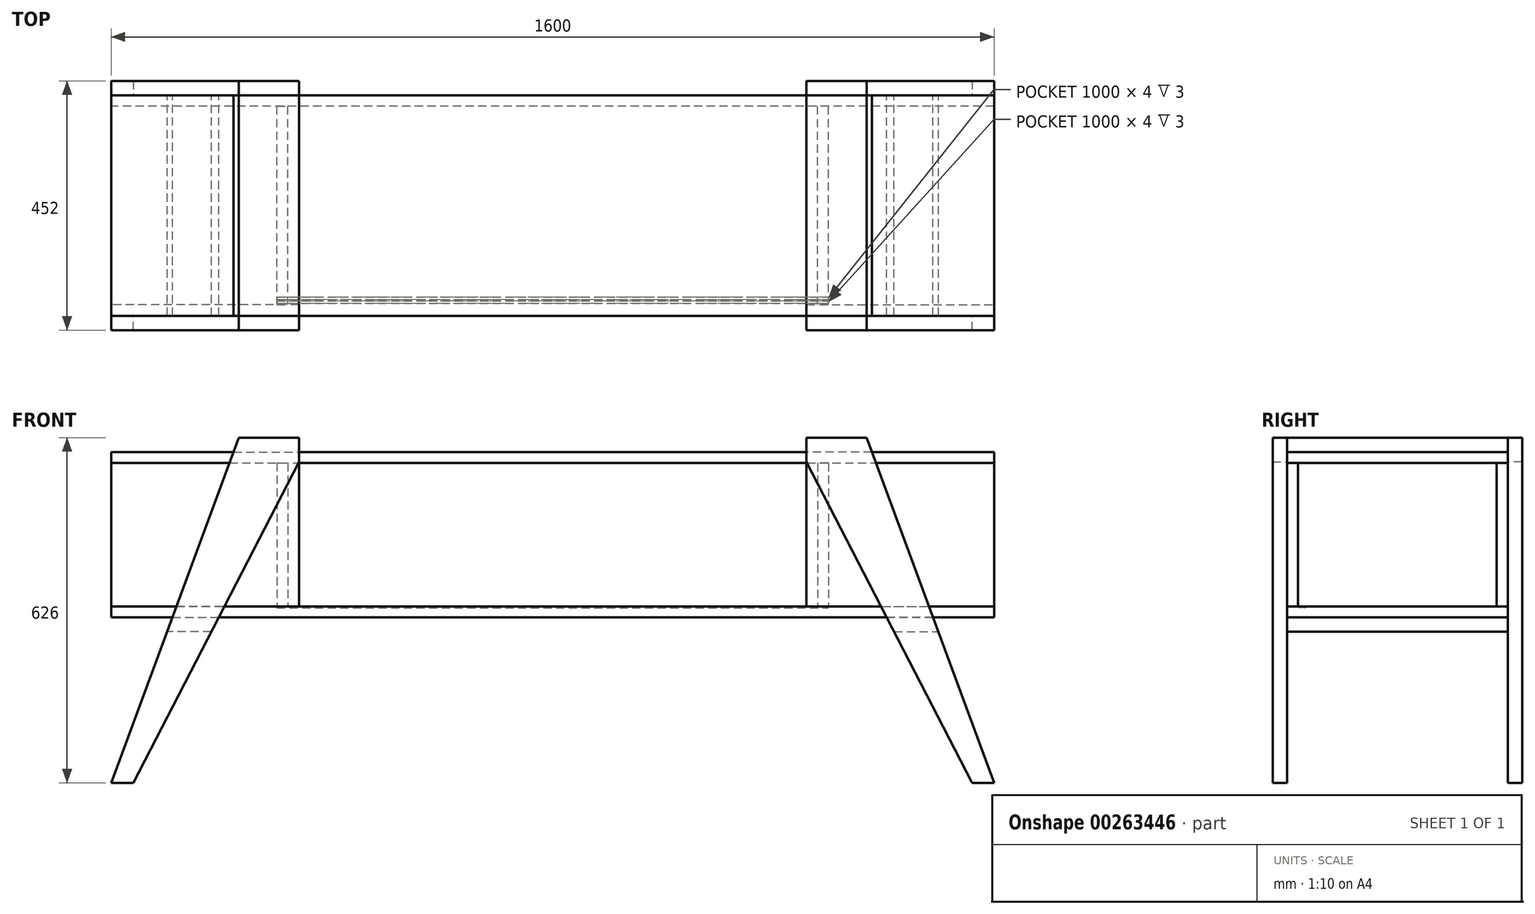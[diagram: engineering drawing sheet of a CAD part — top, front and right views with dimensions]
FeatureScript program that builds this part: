
annotation { "Feature Type Name" : "Feature", "Feature Type Description" : "" }
export const myFeature = defineFeature(function(context is Context, id is Id, definition is map)
    precondition{}
    {
        {
            assignVariable(context, id + "F0", {"name" : "Long", "anyValue" : 1600});
        }
        {
            assignVariable(context, id + "F1", {"name" : "Prof", "anyValue" : 400});
        }
        {
            assignVariable(context, id + "F2", {"name" : "EpP", "anyValue" : 20});
        }
        {
            assignVariable(context, id + "F3", {"name" : "EpFoot", "anyValue" : 26});
        }
        {
            assignVariable(context, id + "F4", {"name" : "EpPortes", "anyValue" : 3});
        }
        {
            var Q0;
            Q0=qCreatedBy(makeId("Front.planeOp"),FACE);
            var sketch = newSketch(context, id + "F5", { "sketchPlane" : qUnion([Q0])});
            skLineSegment(sketch, "E0.bottom", {"start": v(-800, 580) * mm, "end": v(800, 580) * mm});
            skLineSegment(sketch, "E0.top", {"start": v(-800, 600) * mm, "end": v(800, 600) * mm});
            skLineSegment(sketch, "E0.left", {"start": v(-800, 580) * mm, "end": v(-800, 600) * mm});
            skLineSegment(sketch, "E0.right", {"start": v(800, 580) * mm, "end": v(800, 600) * mm});
            skLineSegment(sketch, "E1", {"start": v(-1523.7, 450) * mm, "end": v(1632.53, 450) * mm, "construction": true});
            skLineSegment(sketch, "E2.MirrorCS", {"start": v(-800, 320) * mm, "end": v(-800, 300) * mm});
            skLineSegment(sketch, "E3.MirrorCS", {"start": v(800, 320) * mm, "end": v(800, 300) * mm});
            skLineSegment(sketch, "E4.MirrorCS", {"start": v(-800, 300) * mm, "end": v(800, 300) * mm});
            skLineSegment(sketch, "E5.MirrorCS", {"start": v(-800, 320) * mm, "end": v(800, 320) * mm});
            skSolve(sketch);
        }
        {
            var Q0;
            Q0=qSketchRegion(id+"F5",true);
            extrude(context, id + "F6", {"entities" : qUnion([Q0]), "endBound" : BoundingType.SYMMETRIC, "depth" : (getVariable(context, 'Prof')) * mm});
        }
        {
            var Q0;
            Q0=qCreatedBy(makeId("Right.planeOp"),FACE);
            var sketch = newSketch(context, id + "F7", { "sketchPlane" : qUnion([Q0])});
            skLineSegment(sketch, "E6.bottom", {"start": v(200, 580) * mm, "end": v(180, 580) * mm});
            skLineSegment(sketch, "E6.top", {"start": v(200, 320) * mm, "end": v(180, 320) * mm});
            skLineSegment(sketch, "E6.left", {"start": v(200, 580) * mm, "end": v(200, 320) * mm});
            skLineSegment(sketch, "E6.right", {"start": v(180, 580) * mm, "end": v(180, 320) * mm});
            skSolve(sketch);
        }
        {
            var Q0;
            Q0=qSketchRegion(id+"F7",true);
            extrude(context, id + "F8", {"entities" : qUnion([Q0]), "endBound" : BoundingType.SYMMETRIC, "depth" : getVariable(context, 'Long') * mm});
        }
        {
            var Q0;
            Q0=qCreatedBy(makeId("Front.planeOp"),FACE);
            var sketch = newSketch(context, id + "F9", { "sketchPlane" : qUnion([Q0])});
            skLineSegment(sketch, "E7.bottom", {"start": v(-500, 580) * mm, "end": v(-480, 580) * mm});
            skLineSegment(sketch, "E7.top", {"start": v(-500, 320) * mm, "end": v(-480, 320) * mm});
            skLineSegment(sketch, "E7.left", {"start": v(-500, 580) * mm, "end": v(-500, 320) * mm});
            skLineSegment(sketch, "E7.right", {"start": v(-480, 580) * mm, "end": v(-480, 320) * mm});
            skSolve(sketch);
        }
        {
            var Q0;
            Q0=qSketchRegion(id+"F9",true);
            extrude(context, id + "F10", {"entities" : qUnion([Q0]), "endBound" : BoundingType.SYMMETRIC, "depth" : (getVariable(context, 'Prof') - 2 * getVariable(context, 'EpP')) * mm});
        }
        {
            var Q0;
            Q0=makeQuery(id+"F10.opExtrude","SWEPT_BODY",BODY,{"disambiguationData":[OSD([sQuery(id+"F9.wireOp",EDGE,"E7.bottom"),sQuery(id+"F9.wireOp",EDGE,"E7.top"),sQuery(id+"F9.wireOp",EDGE,"E7.left"),sQuery(id+"F9.wireOp",EDGE,"E7.right")])]});
            var Q1;
            Q1=qCreatedBy(makeId("Right.planeOp"),FACE);
            mirror(context, id + "F11", {"entities" : qUnion([Q0]), "mirrorPlane" : qUnion([Q1])});
        }
        {
            var Q0;
            Q0=makeQuery(id+"F10.opExtrude","SWEPT_FACE",FACE,{"disambiguationData":[OSD([sQuery(id+"F9.wireOp",EDGE,"E7.right")])]});
            var sketch = newSketch(context, id + "F12", { "sketchPlane" : qUnion([Q0])});
            skLineSegment(sketch, "E8.bottom", {"start": v(-200, 580) * mm, "end": v(-180, 580) * mm});
            skLineSegment(sketch, "E8.top", {"start": v(-200, 320) * mm, "end": v(-180, 320) * mm});
            skLineSegment(sketch, "E8.left", {"start": v(-200, 580) * mm, "end": v(-200, 320) * mm});
            skLineSegment(sketch, "E8.right", {"start": v(-180, 580) * mm, "end": v(-180, 320) * mm});
            skSolve(sketch);
        }
        {
            var Q0;
            Q0=qSketchRegion(id+"F12",true);
            var Q1;
            Q1=makeQuery(id+"F6.opExtrude","SWEPT_FACE",FACE,{"disambiguationData":[OSD([sQuery(id+"F5.wireOp",EDGE,"E0.left")])]});
            extrude(context, id + "F13", {"entities" : qUnion([Q0]), "depth" : (getVariable(context, 'EpP')) * mm, "hasSecondDirection" : true, "secondDirectionBound" : SecondDirectionBoundingType.UP_TO_SURFACE, "secondDirectionOppositeDirection" : true, "secondDirectionBoundEntityFace" : qUnion([Q1]), "secondDirectionDepth" : 25 * mm});
        }
        {
            var Q0;
            Q0=makeQuery(id+"F13.opExtrude","SWEPT_BODY",BODY,{"disambiguationData":[OSD([sQuery(id+"F12.wireOp",EDGE,"E8.bottom"),sQuery(id+"F12.wireOp",EDGE,"E8.top"),sQuery(id+"F12.wireOp",EDGE,"E8.left"),sQuery(id+"F12.wireOp",EDGE,"E8.right")])]});
            var Q1;
            Q1=qCreatedBy(makeId("Right.planeOp"),FACE);
            mirror(context, id + "F14", {"entities" : qUnion([Q0]), "mirrorPlane" : qUnion([Q1])});
        }
        {
            var Q0;
            Q0=makeQuery(id+"F6.opExtrude","SWEPT_FACE",FACE,{"disambiguationData":[OSD([sQuery(id+"F5.wireOp",EDGE,"E5.MirrorCS")])]});
            var sketch = newSketch(context, id + "F15", { "sketchPlane" : qUnion([Q0])});
            skLineSegment(sketch, "E9.bottom", {"start": v(-500, -173) * mm, "end": v(500, -173) * mm});
            skLineSegment(sketch, "E9.top", {"start": v(-500, -177) * mm, "end": v(500, -177) * mm});
            skLineSegment(sketch, "E9.left", {"start": v(-500, -173) * mm, "end": v(-500, -177) * mm});
            skLineSegment(sketch, "E9.right", {"start": v(500, -173) * mm, "end": v(500, -177) * mm});
            skLineSegment(sketch, "E10.bottom", {"start": v(-500, -166) * mm, "end": v(500, -166) * mm});
            skLineSegment(sketch, "E10.top", {"start": v(-500, -170) * mm, "end": v(500, -170) * mm});
            skLineSegment(sketch, "E10.left", {"start": v(-500, -166) * mm, "end": v(-500, -170) * mm});
            skLineSegment(sketch, "E10.right", {"start": v(500, -166) * mm, "end": v(500, -170) * mm});
            skSolve(sketch);
        }
        {
            var Q0;
            Q0=qSketchRegion(id+"F15",true);
            extrude(context, id + "F16", {"entities" : qUnion([Q0]), "operationType" : NewBodyOperationType.REMOVE, "oppositeDirection" : true, "depth" : (getVariable(context, 'EpPortes')) * mm});
        }
        {
            var Q0;
            Q0=makeQuery(id+"F6.opExtrude","CAP_FACE",FACE,{"disambiguationData":[OSD([sQuery(id+"F5.wireOp",EDGE,"E2.MirrorCS"),sQuery(id+"F5.wireOp",EDGE,"E3.MirrorCS"),sQuery(id+"F5.wireOp",EDGE,"E4.MirrorCS"),sQuery(id+"F5.wireOp",EDGE,"E5.MirrorCS")])],"isStart":false});
            var sketch = newSketch(context, id + "F17", { "sketchPlane" : qUnion([Q0])});
            skLineSegment(sketch, "E11", {"start": v(-800, 0) * mm, "end": v(-568.8, 626) * mm});
            skLineSegment(sketch, "E12", {"start": v(-568.8, 626) * mm, "end": v(-460, 626) * mm});
            skLineSegment(sketch, "E13", {"start": v(-460, 581.97) * mm, "end": v(-760, 0) * mm});
            skLineSegment(sketch, "E14", {"start": v(-760, 0) * mm, "end": v(-800, 0) * mm});
            skLineSegment(sketch, "E15", {"start": v(-460, 626) * mm, "end": v(-460, 581.97) * mm});
            skSolve(sketch);
        }
        {
            var Q0;
            Q0=qSketchRegion(id+"F17",true);
            extrude(context, id + "F18", {"entities" : qUnion([Q0]), "depth" : (getVariable(context, 'EpFoot')) * mm});
        }
        {
            var Q0;
            Q0=makeQuery(id+"F18.opExtrude","SWEPT_BODY",BODY,{"disambiguationData":[OSD([sQuery(id+"F17.wireOp",EDGE,"E11"),sQuery(id+"F17.wireOp",EDGE,"E12"),sQuery(id+"F17.wireOp",EDGE,"E13"),sQuery(id+"F17.wireOp",EDGE,"E14")])]});
            var Q1;
            Q1=qCreatedBy(makeId("Right.planeOp"),FACE);
            mirror(context, id + "F19", {"entities" : qUnion([Q0]), "mirrorPlane" : qUnion([Q1])});
        }
        {
            var Q0;
            Q0=makeQuery(id+"F18.opExtrude","SWEPT_BODY",BODY,{"disambiguationData":[OSD([sQuery(id+"F17.wireOp",EDGE,"E11"),sQuery(id+"F17.wireOp",EDGE,"E12"),sQuery(id+"F17.wireOp",EDGE,"E13"),sQuery(id+"F17.wireOp",EDGE,"E14")])]});
            var Q1;
            Q1=qCreatedBy(makeId("Front.planeOp"),FACE);
            mirror(context, id + "F20", {"entities" : qUnion([Q0]), "mirrorPlane" : qUnion([Q1])});
        }
        {
            var Q0;
            Q0=makeQuery(id+"F19.opPattern","COPY",BODY,{"derivedFrom":makeQuery(id+"F18.opExtrude","SWEPT_BODY",BODY,{"disambiguationData":[OSD([sQuery(id+"F17.wireOp",EDGE,"E11"),sQuery(id+"F17.wireOp",EDGE,"E12"),sQuery(id+"F17.wireOp",EDGE,"E13"),sQuery(id+"F17.wireOp",EDGE,"E14")])]}),"instanceName":"1"});
            var Q1;
            Q1=qCreatedBy(makeId("Front.planeOp"),FACE);
            mirror(context, id + "F21", {"entities" : qUnion([Q0]), "mirrorPlane" : qUnion([Q1])});
        }
        {
            var Q0;
            Q0=makeQuery(id+"F20.opPattern","COPY",FACE,{"derivedFrom":makeQuery(id+"F18.opExtrude","CAP_FACE",FACE,{"disambiguationData":[OSD([sQuery(id+"F17.wireOp",EDGE,"E11"),sQuery(id+"F17.wireOp",EDGE,"E12"),sQuery(id+"F17.wireOp",EDGE,"E13"),sQuery(id+"F17.wireOp",EDGE,"E14")])],"isStart":true}),"instanceName":"1"});
            var sketch = newSketch(context, id + "F22", { "sketchPlane" : qUnion([Q0])});
            skLineSegment(sketch, "E16", {"start": v(-578.4, 600) * mm, "end": v(-568.8, 626) * mm});
            skLineSegment(sketch, "E17", {"start": v(-568.8, 626) * mm, "end": v(-568.8, 626) * mm});
            skLineSegment(sketch, "E18", {"start": v(-568.8, 626) * mm, "end": v(-460, 626) * mm});
            skLineSegment(sketch, "E19", {"start": v(-578.4, 600) * mm, "end": v(-460, 600) * mm});
            skLineSegment(sketch, "E20", {"start": v(-460, 600) * mm, "end": v(-460, 626) * mm});
            skSolve(sketch);
        }
        {
            var Q0;
            Q0=qSketchRegion(id+"F22",true);
            var Q1;
            Q1=makeQuery(id+"F18.opExtrude","CAP_FACE",FACE,{"disambiguationData":[OSD([sQuery(id+"F17.wireOp",EDGE,"E11"),sQuery(id+"F17.wireOp",EDGE,"E12"),sQuery(id+"F17.wireOp",EDGE,"E13"),sQuery(id+"F17.wireOp",EDGE,"E14")])],"isStart":true});
            extrude(context, id + "F23", {"entities" : qUnion([Q0]), "endBound" : BoundingType.UP_TO_SURFACE, "endBoundEntityFace" : qUnion([Q1]), "depth" : 25 * mm});
        }
        {
            var Q0;
            Q0=makeQuery(id+"F23.opExtrude","SWEPT_BODY",BODY,{"disambiguationData":[OSD([sQuery(id+"F22.wireOp",EDGE,"E16"),sQuery(id+"F22.wireOp",EDGE,"E17"),sQuery(id+"F22.wireOp",EDGE,"E18"),sQuery(id+"F22.wireOp",EDGE,"Wh4QzbhV-d2Ks-FXWY-guVt-hGYjwTEAgDKb")])]});
            var Q1;
            Q1=qCreatedBy(makeId("Right.planeOp"),FACE);
            mirror(context, id + "F24", {"entities" : qUnion([Q0]), "mirrorPlane" : qUnion([Q1])});
        }
        {
            var Q0;
            Q0=makeQuery(id+"F20.opPattern","COPY",FACE,{"derivedFrom":makeQuery(id+"F18.opExtrude","CAP_FACE",FACE,{"disambiguationData":[OSD([sQuery(id+"F17.wireOp",EDGE,"E11"),sQuery(id+"F17.wireOp",EDGE,"E12"),sQuery(id+"F17.wireOp",EDGE,"E13"),sQuery(id+"F17.wireOp",EDGE,"E14"),sQuery(id+"F17.wireOp",EDGE,"E15")])],"isStart":true}),"instanceName":"1"});
            var sketch = newSketch(context, id + "F25", { "sketchPlane" : qUnion([Q0])});
            skLineSegment(sketch, "E21", {"start": v(-689.2, 300) * mm, "end": v(-605.35, 300) * mm});
            skLineSegment(sketch, "E22", {"start": v(-605.35, 300) * mm, "end": v(-618.76, 274) * mm});
            skLineSegment(sketch, "E23", {"start": v(-618.76, 274) * mm, "end": v(-698.8, 274) * mm});
            skLineSegment(sketch, "E24", {"start": v(-698.8, 274) * mm, "end": v(-689.2, 300) * mm});
            skSolve(sketch);
        }
        {
            var Q0;
            Q0 = qSketchRegion(id + "F25", true);
            var Q1;
            Q1=makeQuery(id+"F18.opExtrude","CAP_FACE",FACE,{"disambiguationData":[OSD([sQuery(id+"F17.wireOp",EDGE,"E11"),sQuery(id+"F17.wireOp",EDGE,"E12"),sQuery(id+"F17.wireOp",EDGE,"E13"),sQuery(id+"F17.wireOp",EDGE,"E14"),sQuery(id+"F17.wireOp",EDGE,"E15")])],"isStart":true});
            extrude(context, id + "F26", {"entities" : qUnion([Q0]), "endBound" : BoundingType.UP_TO_SURFACE, "endBoundEntityFace" : qUnion([Q1]), "depth" : 25 * mm});
        }
        {
            var Q0;
            Q0=makeQuery(id+"F26.opExtrude","SWEPT_BODY",BODY,{"disambiguationData":[OSD([sQuery(id+"F25.wireOp",EDGE,"E21"),sQuery(id+"F25.wireOp",EDGE,"E22"),sQuery(id+"F25.wireOp",EDGE,"E23"),sQuery(id+"F25.wireOp",EDGE,"E24")])]});
            var Q1;
            Q1=qCreatedBy(makeId("Right.planeOp"),FACE);
            mirror(context, id + "F27", {"entities" : qUnion([Q0]), "mirrorPlane" : qUnion([Q1])});
        }
    });
